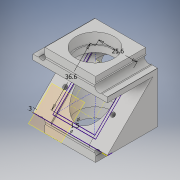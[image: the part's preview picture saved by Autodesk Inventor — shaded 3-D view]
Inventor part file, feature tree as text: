
AUTODESK INVENTOR PART (.ipt)
format: ipt  version: 2019 (Build 230136000, 136)  size: 476,672 bytes
history: native  units: mm
features: sketch x15, extrude x14, reference x12, projected_geometry x9, other x7, plane x3, mirror x2, pattern_circular x1
ambient origin geometry x8: Origin, YZ Plane, XZ Plane, XY Plane, X Axis, Y Axis, Z Axis, Center Point
bodies: Solid1 (feature_tree)
feature tree (63):
  extrude  "Extrusion1"  Depth=24.9mm
  sketch  "Sketch6"  dims[d20=3.14mm d21=26.9mm]
  plane  "Work Plane2"
  extrude  "Extrusion6"  Depth=26.9mm
  extrude  "Extrusion7"  Depth=3.0mm TaperAngle=0.0deg
  sketch  "Sketch8"  dims[d41=10.0mm d42=0.0mm d43=0.0mm d44=0.0mm]
  extrude  "Extrusion8"  TaperAngle=0.0deg  [1 undecoded]
  extrude  "Extrusion9"  Depth=15.0mm
  extrude  "Extrusion10"  Depth=10.0mm
  sketch  "Sketch12"  dims[d50=7.0mm d51=0.0mm d52=25.5mm]
  sketch  "Sketch13"  dims[d53=7.0mm d54=0.0mm d59=1.0mm d60=0.0mm]
  plane  "Work Plane3"
  extrude  "Extrusion12"  Depth=25.5mm
  extrude  "Extrusion13"  Depth=1.0mm TaperAngle=0.0deg
  extrude  "Extrusion14"  Depth=7.0mm TaperAngle=0.0deg
  extrude  "Extrusion15"  Depth=2.8mm
  extrude  "Extrusion16"  Depth=5.0mm TaperAngle=0.0deg
  extrude  "Extrusion17"  TaperAngle=0.0deg  [1 undecoded]
  mirror  "Mirror3"
  mirror  "Mirror4"
  pattern_circular  "Circular Pattern1"  Count=4 Angle=360.0deg
  plane  "Work Plane4"
  extrude  "Extrusion18"  Depth=10.0mm
  extrude  "Extrusion19"  Depth=10.0mm
  sketch  "Sketch1"  dims[d17=45.0deg d18=24.9mm]
  projected_geometry  "Projected Loop6"
  sketch  "Sketch7"  dims[d22=15.0mm d23=3.0mm d24=0.0mm]
  reference  "Reference1"
  reference  "Reference2"
  reference  "Reference3"
  reference  "Reference4"
  reference  "Reference5"
  reference  "Reference6"
  reference  "Reference7"
  sketch  "Sketch10"  dims[d45=3.0mm d46=15.0mm]
  sketch  "Sketch11"  dims[d47=10.0mm d48=0.0mm d49=25.5mm]
  reference  "Reference8"
  reference  "Reference9"
  reference  "Reference10"
  reference  "Reference11"
  projected_geometry  "Projected Loop7"
  sketch  "Sketch14"  dims[d61=25.5mm d62=7.0mm d63=0.0mm]
  reference  "Reference12"
  sketch  "Sketch15"  dims[d64=5.0mm d65=0.0mm d68=2.8mm]
  sketch  "Sketch16"  dims[d69=2.8mm d70=5.0mm d71=0.0mm]
  projected_geometry  "Projected Loop8"
  sketch  "Sketch17"  dims[d72=33.5mm d73=0.0mm d74=0.0mm]
  sketch  "Sketch18"  dims[d75=5.0mm]
  projected_geometry  "Projected Loop9"
  projected_geometry  "Projected Loop10"
  sketch  "Sketch19"  dims[d76=10.0mm d77=0.0mm d78=40.0mm d79=360.0deg]
  projected_geometry  "Projected Loop11"
  sketch  "Sketch20"  dims[d81=25.6mm d82=36.6mm d83=1.5mm d84=24.0mm d85=16.0mm d86=16.0mm d87=2.0mm d88=0.0mm d89=0.2mm d90=10.0mm d91=0.0mm]
  projected_geometry  "Projected Loop12"
  projected_geometry  "Projected Loop13"
  projected_geometry  "Projected Loop14"
  other  "Assembly_Cube_Dichroic_Beamsplitter_25x35.iam"
  other  "Assembly_Cube_empty_1x1_v2:1"
  other  "10_Lid_1x1_v2:1"
  other  "Assembly_Cube_Dichroic_Beamsplitter.iam"
  other  "00_Comar_Filter_25Dia:1"
  other  "10_Cube_1x1_v2:1"
  other  "00_Comar_Dichroic_16x25x0.2:1"
note: 2 required parameter values undecoded (feature->parameter linkage not recoverable at this tier; creation-order binding heuristic only, values carry confidence <= 0.55)
